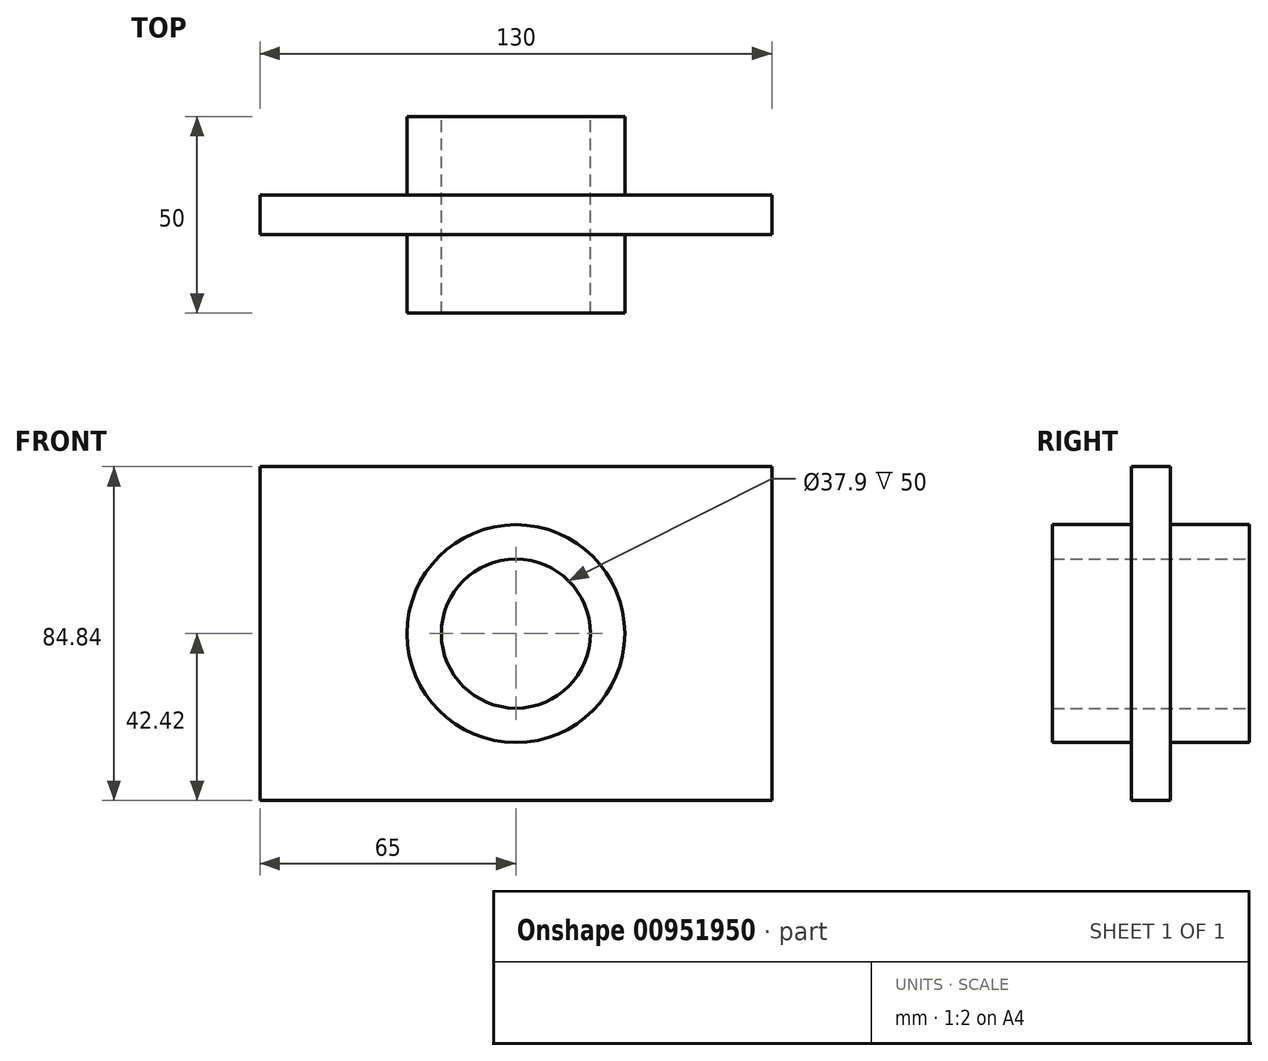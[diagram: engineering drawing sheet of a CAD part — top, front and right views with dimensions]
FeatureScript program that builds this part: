
annotation { "Feature Type Name" : "Feature", "Feature Type Description" : "" }
export const myFeature = defineFeature(function(context is Context, id is Id, definition is map)
    precondition{}
    {
        {
            var Q0;
            Q0=qCreatedBy(makeId("Front.planeOp"),FACE);
            var sketch = newSketch(context, id + "F0", { "sketchPlane" : qUnion([Q0])});
            skArc(sketch, "E0", {"start": v(0, 18.95) * mm, "mid": v(18.95, 0) * mm, "end": v(0, -18.95) * mm});
            skArc(sketch, "E1", {"start": v(0, -27.67) * mm, "mid": v(27.67, 0) * mm, "end": v(0, 27.67) * mm});
            skLineSegment(sketch, "E2", {"start": v(0, 18.95) * mm, "end": v(0, 27.67) * mm});
            skLineSegment(sketch, "E3", {"start": v(0, -18.95) * mm, "end": v(0, -27.67) * mm});
            skSolve(sketch);
        }
        {
            var Q0;
            Q0 = qSketchRegion(id + "F0", true);
            extrude(context, id + "F1", {"entities" : qUnion([Q0]), "endBound" : BoundingType.SYMMETRIC, "depth" : 50 * mm, "offsetDistance" : 25 * mm});
        }
        {
            var Q0;
            Q0=qCreatedBy(makeId("Front.planeOp"),FACE);
            var sketch = newSketch(context, id + "F2", { "sketchPlane" : qUnion([Q0])});
            skArc(sketch, "E4", {"start": v(0, 27.42) * mm, "mid": v(27.42, 0) * mm, "end": v(0, -27.42) * mm});
            skLineSegment(sketch, "E5", {"start": v(0, -27.42) * mm, "end": v(0, -42.42) * mm});
            skLineSegment(sketch, "E6", {"start": v(0, -42.42) * mm, "end": v(65, -42.42) * mm});
            skLineSegment(sketch, "E7", {"start": v(65, -42.42) * mm, "end": v(65, 42.42) * mm});
            skLineSegment(sketch, "E8", {"start": v(65, 42.42) * mm, "end": v(0, 42.42) * mm});
            skLineSegment(sketch, "E9", {"start": v(0, 42.42) * mm, "end": v(0, 27.42) * mm});
            skSolve(sketch);
        }
        {
            var Q0;
            Q0 = qSketchRegion(id + "F2", true);
            extrude(context, id + "F3", {"entities" : qUnion([Q0]), "operationType" : NewBodyOperationType.ADD, "endBound" : BoundingType.SYMMETRIC, "depth" : 10 * mm, "offsetDistance" : 25 * mm});
        }
        {
            var Q0;
            Q0=makeQuery(id+"F1.opExtrude","SWEPT_BODY",BODY,{"disambiguationData":[OSD([sQuery(id+"F0.wireOp",EDGE,"E0"),sQuery(id+"F0.wireOp",EDGE,"E1"),sQuery(id+"F0.wireOp",EDGE,"E2"),sQuery(id+"F0.wireOp",EDGE,"E3")])]});
            var Q1;
            Q1=makeQuery(id+"F3.boolean.opBoolean","MERGE",FACE,{"derivedFrom":[makeQuery(id+"F1.opExtrude","SWEPT_FACE",FACE,{"disambiguationData":[OSD([sQuery(id+"F0.wireOp",EDGE,"E2")])]}),makeQuery(id+"F3.opExtrude","SWEPT_FACE",FACE,{"disambiguationData":[OSD([sQuery(id+"F2.wireOp",EDGE,"E9")])]})]});
            mirror(context, id + "F4", {"operationType" : NewBodyOperationType.ADD, "entities" : qUnion([Q0]), "mirrorPlane" : qUnion([Q1])});
        }
    });
